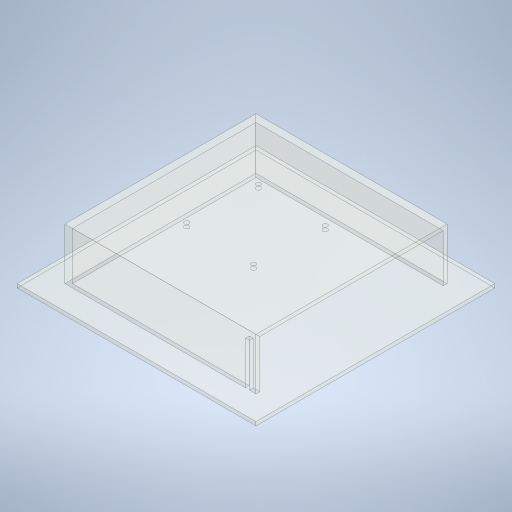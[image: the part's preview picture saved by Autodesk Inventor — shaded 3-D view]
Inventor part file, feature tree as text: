
AUTODESK INVENTOR PART (.ipt)
format: ipt  version: 2024 (Build 280153000, 153)  size: 294,400 bytes
history: native  units: in
note: dims shown in document units (in); Inventor stores cm internally (conversion verified against a paired STEP export)
features: sketch x6, extrude x5, hole x1
ambient origin geometry x8: Origin, YZ Plane, XZ Plane, XY Plane, X Axis, Y Axis, Z Axis, Center Point
bodies: Solid1 (feature_tree)
feature tree (12):
  extrude  "Main Body Extrusion"  Depth=7.5591in
  extrude  "Extrusion3"  Depth=7.874in
  extrude  "Extrusion8"  Depth=0.1575in
  extrude  "Extrusion9"  Depth=0.1575in
  extrude  "Extrusion10"  Depth=1.7717in TaperAngle=0.0deg
  hole  "Hole1"  [1 undecoded]
  sketch  "Sketch1"  dims[d13=1.9685in d14=0.0in d16=7.5591in]
  sketch  "Sketch3"  dims[d17=7.874in d18=7.874in]
  sketch  "Sketch8"  dims[d35=0.0787in d36=0.0in d39=0.1575in]
  sketch  "Sketch9"  dims[d40=7.2835in d41=0.1575in]
  sketch  "Sketch10"  dims[d42=1.7717in d43=0.0787in d44=0.0in]
  sketch  "Sketch11"  dims[d45=0.1575in d46=0.0in d47=0.1575in d48=0.1575in d49=0.1969in d50=0.2953in d51=0.1476in d52=0.0984in d53=90.0deg d54=0.3937in d55=0.0in d56=3.937in d57=3.937in d58=0.4921in d59=0.5906in d60=1.5748in d62=360.0deg]
note: 1 required parameter value undecoded (feature->parameter linkage not recoverable at this tier; creation-order binding heuristic only, values carry confidence <= 0.55)
